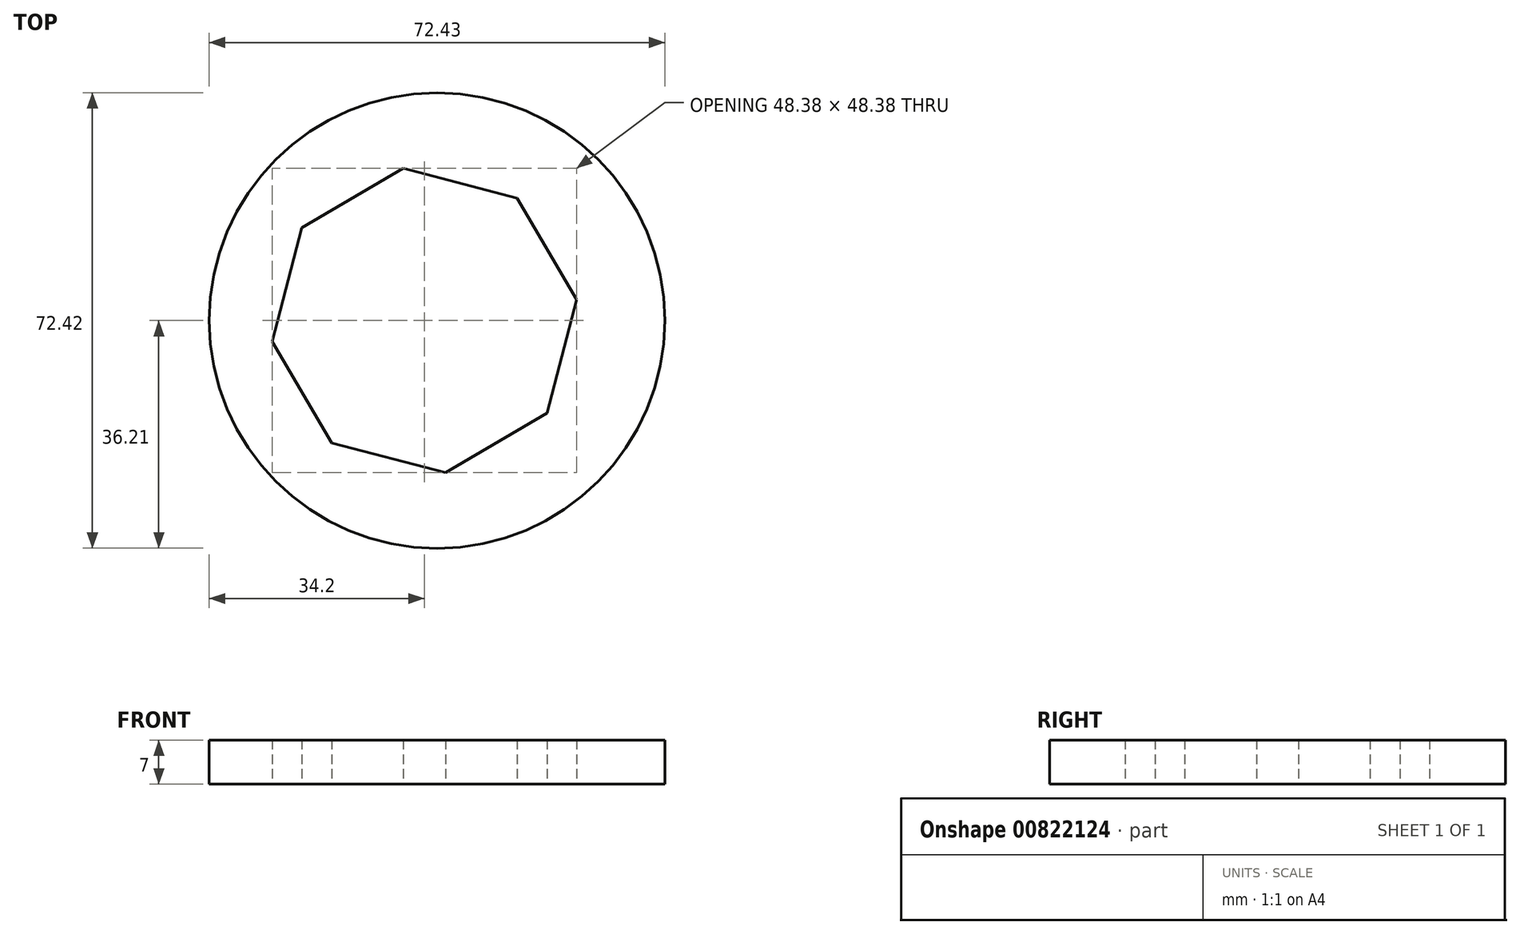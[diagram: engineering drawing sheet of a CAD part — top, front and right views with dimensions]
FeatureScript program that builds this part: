
annotation { "Feature Type Name" : "Feature", "Feature Type Description" : "" }
export const myFeature = defineFeature(function(context is Context, id is Id, definition is map)
    precondition{}
    {
        {
            var Q0;
            Q0=qCreatedBy(makeId("Top.planeOp"),FACE);
            var sketch = newSketch(context, id + "F0", { "sketchPlane" : qUnion([Q0])});
            skCircle(sketch, "E0", {"center": v(2.01, 0) * mm, "radius": 36.21 * mm});
            skCircle(sketch, "E1.cCircle", {"center": v(0, 0) * mm, "radius": 22.56 * mm, "construction": true});
            skLineSegment(sketch, "E1.0", {"start": v(-14.74, -19.47) * mm, "end": v(-24.2, -3.35) * mm});
            skLineSegment(sketch, "E1.1", {"start": v(-24.2, -3.35) * mm, "end": v(-19.47, 14.74) * mm});
            skLineSegment(sketch, "E1.2", {"start": v(-19.47, 14.74) * mm, "end": v(-3.35, 24.2) * mm});
            skLineSegment(sketch, "E1.3", {"start": v(-3.35, 24.2) * mm, "end": v(14.74, 19.47) * mm});
            skLineSegment(sketch, "E1.4", {"start": v(14.74, 19.47) * mm, "end": v(24.2, 3.35) * mm});
            skLineSegment(sketch, "E1.5", {"start": v(24.2, 3.35) * mm, "end": v(19.47, -14.74) * mm});
            skLineSegment(sketch, "E1.6", {"start": v(19.47, -14.74) * mm, "end": v(3.35, -24.2) * mm});
            skLineSegment(sketch, "E1.7", {"start": v(3.35, -24.2) * mm, "end": v(-14.74, -19.47) * mm});
            skPoint(sketch, "E1.0.midPoint", {"position": v(-19.47, -11.41) * mm});
            skSolve(sketch);
        }
        {
            var Q0;
            Q0 = qSketchRegion(id + "F0", true);
            extrude(context, id + "F1", {"entities" : qUnion([Q0]), "depth" : 7 * mm, "offsetDistance" : 25.4 * mm});
        }
    });
